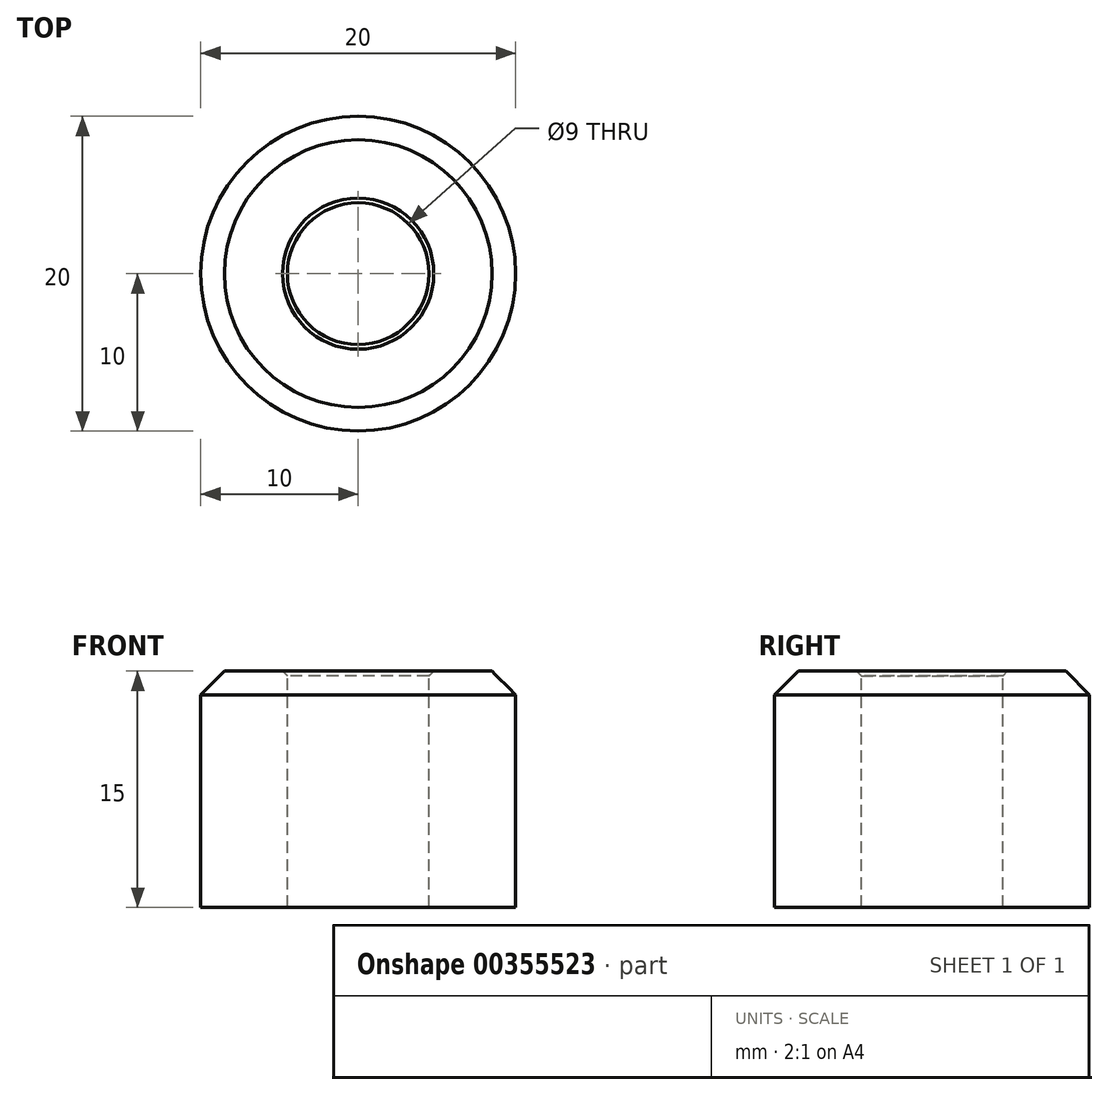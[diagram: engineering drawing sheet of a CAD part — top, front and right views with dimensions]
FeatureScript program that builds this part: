
annotation { "Feature Type Name" : "Feature", "Feature Type Description" : "" }
export const myFeature = defineFeature(function(context is Context, id is Id, definition is map)
    precondition{}
    {
        {
            var Q0;
            Q0=qCreatedBy(makeId("Top.planeOp"),FACE);
            var sketch = newSketch(context, id + "F0", { "sketchPlane" : qUnion([Q0])});
            skCircle(sketch, "E0", {"center": v(0, 0) * mm, "radius": 10 * mm});
            skCircle(sketch, "E1", {"center": v(0, 0) * mm, "radius": 4.5 * mm});
            skSolve(sketch);
        }
        {
            var Q0;
            Q0 = qSketchRegion(id + "F0", true);
            extrude(context, id + "F1", {"entities" : qUnion([Q0]), "oppositeDirection" : true, "depth" : 15 * mm});
        }
        {
            var Q0;
            Q0=makeQuery(id+"F1.opExtrude","CAP_EDGE",EDGE,{"disambiguationData":[OSD([sQuery(id+"F0.wireOp",EDGE,"E0")])],"isStart":true});
            chamfer(context, id + "F2", {"entities" : qUnion([Q0]), "width" : 1.5 * mm, "tangentPropagation" : true});
        }
        {
            var Q0;
            Q0=makeQuery(id+"F1.opExtrude","CAP_EDGE",EDGE,{"disambiguationData":[OSD([sQuery(id+"F0.wireOp",EDGE,"E1")])],"isStart":true});
            chamfer(context, id + "F3", {"entities" : qUnion([Q0]), "width" : 0.3 * mm, "tangentPropagation" : true});
        }
    });
